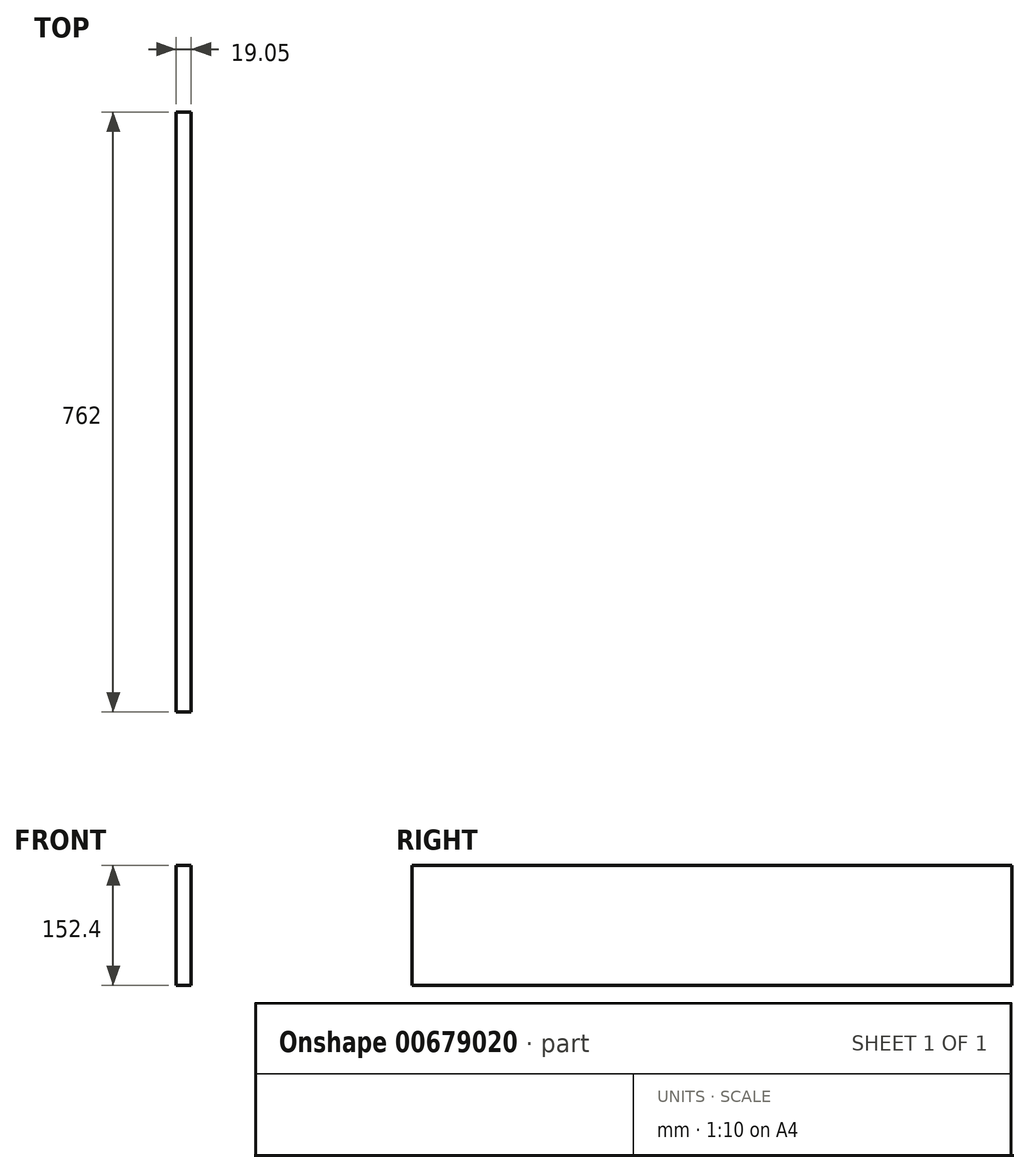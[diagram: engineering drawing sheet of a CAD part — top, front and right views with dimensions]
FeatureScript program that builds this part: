
annotation { "Feature Type Name" : "Feature", "Feature Type Description" : "" }
export const myFeature = defineFeature(function(context is Context, id is Id, definition is map)
    precondition{}
    {
        {
            var Q0;
            Q0=qCreatedBy(makeId("Right.planeOp"),FACE);
            var sketch = newSketch(context, id + "F0", { "sketchPlane" : qUnion([Q0])});
            skLineSegment(sketch, "E0.bottom", {"start": v(381, 76.2) * mm, "end": v(-381, 76.2) * mm});
            skLineSegment(sketch, "E0.top", {"start": v(381, -76.2) * mm, "end": v(-381, -76.2) * mm});
            skLineSegment(sketch, "E0.left", {"start": v(381, 76.2) * mm, "end": v(381, -76.2) * mm});
            skLineSegment(sketch, "E0.right", {"start": v(-381, 76.2) * mm, "end": v(-381, -76.2) * mm});
            skPoint(sketch, "E0.middle", {"position": v(0, 0) * mm});
            skSolve(sketch);
        }
        {
            var Q0;
            Q0=makeQuery(id+"F0.imprint","IMPRINT",FACE,{"disambiguationData":[TD([[makeQuery(id+"F0.imprint","IMPRINT",EDGE,{"derivedFrom":sQuery(id+"F0.wireOp",EDGE,"E0.bottom")}),1.0]])]});
            extrude(context, id + "F1", {"entities" : qUnion([Q0]), "depth" : 19.05 * mm, "offsetDistance" : 25.4 * mm});
        }
    });
